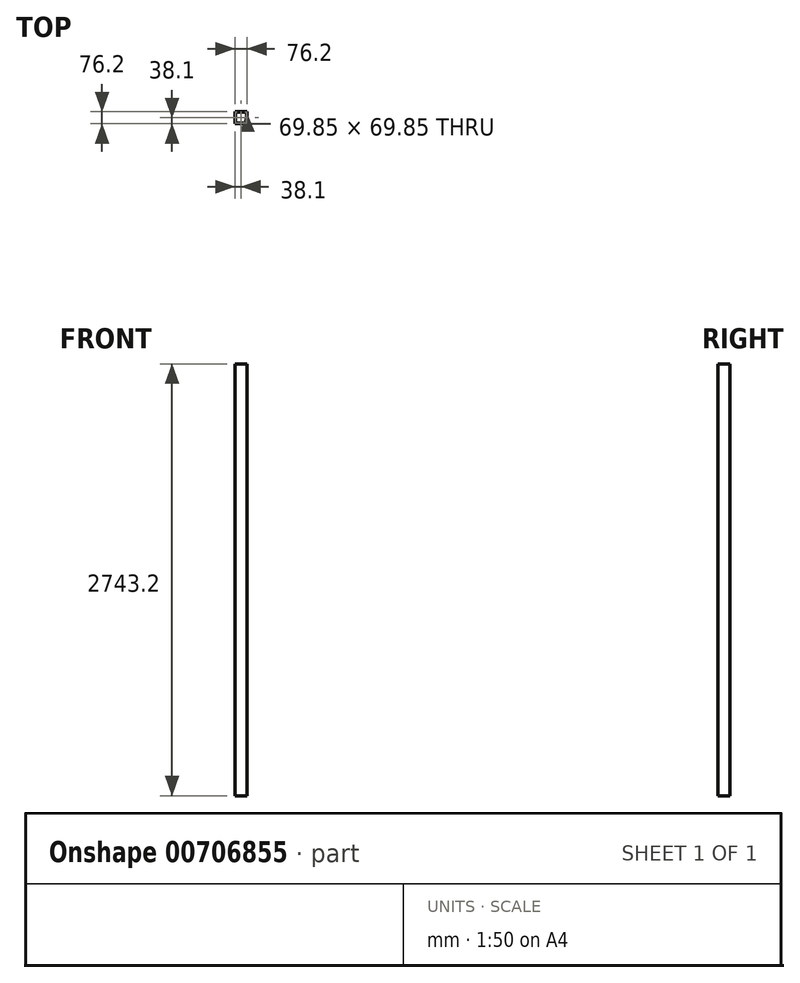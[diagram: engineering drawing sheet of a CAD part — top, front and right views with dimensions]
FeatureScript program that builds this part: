
annotation { "Feature Type Name" : "Feature", "Feature Type Description" : "" }
export const myFeature = defineFeature(function(context is Context, id is Id, definition is map)
    precondition{}
    {
        {
            var Q0;
            Q0=qCreatedBy(makeId("Top.planeOp"),FACE);
            var sketch = newSketch(context, id + "F0", { "sketchPlane" : qUnion([Q0])});
            skLineSegment(sketch, "E0.bottom", {"start": v(-38.1, 38.1) * mm, "end": v(38.1, 38.1) * mm});
            skLineSegment(sketch, "E0.top", {"start": v(-38.1, -38.1) * mm, "end": v(38.1, -38.1) * mm});
            skLineSegment(sketch, "E0.left", {"start": v(-38.1, 38.1) * mm, "end": v(-38.1, -38.1) * mm});
            skLineSegment(sketch, "E0.right", {"start": v(38.1, 38.1) * mm, "end": v(38.1, -38.1) * mm});
            skLineSegment(sketch, "E1.bottom", {"start": v(-34.92, 34.93) * mm, "end": v(34.92, 34.93) * mm});
            skLineSegment(sketch, "E1.top", {"start": v(-34.92, -34.93) * mm, "end": v(34.92, -34.93) * mm});
            skLineSegment(sketch, "E1.left", {"start": v(-34.92, 34.93) * mm, "end": v(-34.92, -34.93) * mm});
            skLineSegment(sketch, "E1.right", {"start": v(34.92, 34.93) * mm, "end": v(34.92, -34.93) * mm});
            skSolve(sketch);
        }
        {
            var Q0;
            Q0=makeQuery(id+"F0.imprint","IMPRINT",FACE,{"disambiguationData":[TD([[makeQuery(id+"F0.imprint","IMPRINT",EDGE,{"derivedFrom":sQuery(id+"F0.wireOp",EDGE,"E0.bottom")}),-1.0]])]});
            extrude(context, id + "F1", {"entities" : qUnion([Q0]), "depth" : 2743.2 * mm, "offsetDistance" : 25.4 * mm});
        }
    });
